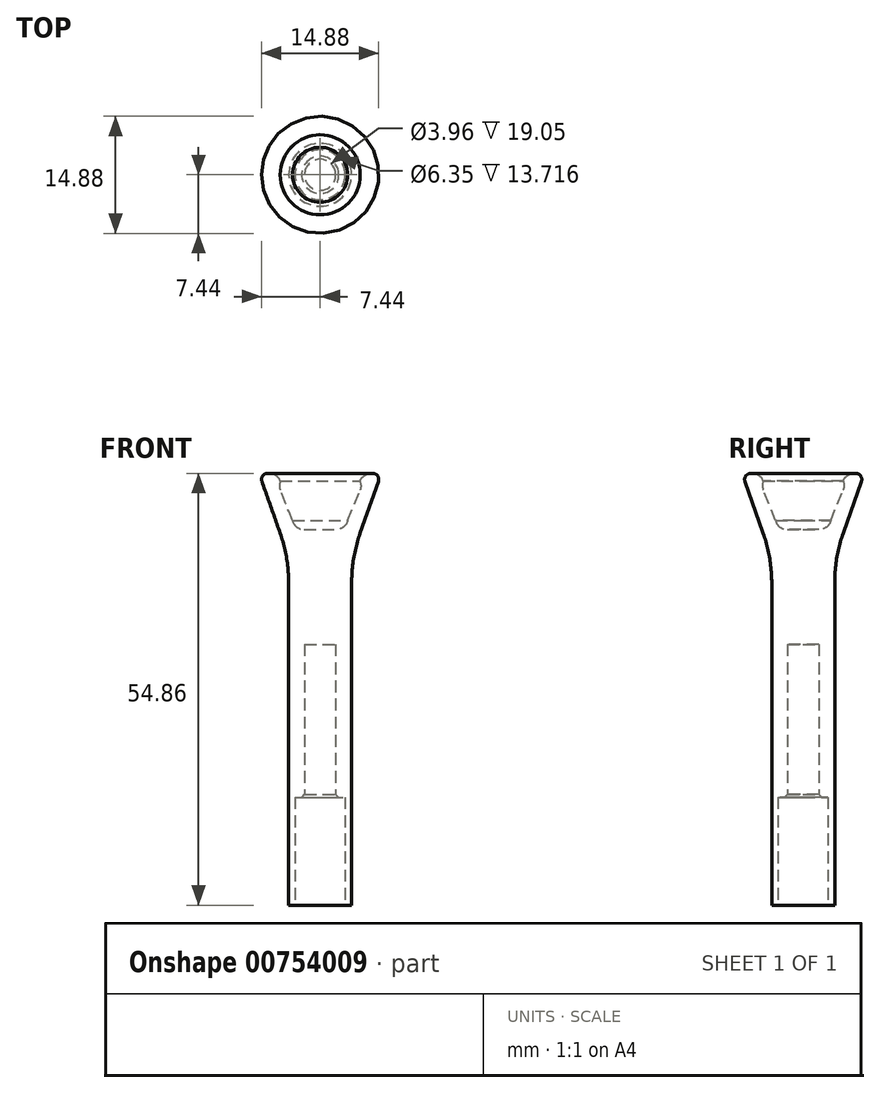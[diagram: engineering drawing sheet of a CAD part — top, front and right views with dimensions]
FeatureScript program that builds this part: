
annotation { "Feature Type Name" : "Feature", "Feature Type Description" : "" }
export const myFeature = defineFeature(function(context is Context, id is Id, definition is map)
    precondition{}
    {
        {
            var Q0;
            Q0=qCreatedBy(makeId("Front.planeOp"),FACE);
            var sketch = newSketch(context, id + "F0", { "sketchPlane" : qUnion([Q0])});
            skLineSegment(sketch, "E0", {"start": v(0, 0) * mm, "end": v(4, 0) * mm});
            skLineSegment(sketch, "E1", {"start": v(4, 0) * mm, "end": v(4, 40.94) * mm});
            skLineSegment(sketch, "E2", {"start": v(0.14, 46.68) * mm, "end": v(0, 46.68) * mm});
            skLineSegment(sketch, "E3", {"start": v(0, 46.68) * mm, "end": v(0, 60.15) * mm});
            skLineSegment(sketch, "E4", {"start": v(2.02, 47.72) * mm, "end": v(0, 47.72) * mm});
            skLineSegment(sketch, "E5", {"start": v(0, 47.72) * mm, "end": v(0, 0) * mm});
            skLineSegment(sketch, "E6", {"start": v(6.49, 54.86) * mm, "end": v(6.68, 54.86) * mm});
            skLineSegment(sketch, "E7", {"start": v(5.08, 47.27) * mm, "end": v(7.4, 53.85) * mm});
            skPoint(sketch, "E8.visualSharp", {"position": v(4, 44.2) * mm});
            skPoint(sketch, "E9.visualSharp", {"position": v(7.76, 54.86) * mm});
            skPoint(sketch, "E10.visualSharp", {"position": v(4.57, 54.86) * mm});
            skArc(sketch, "E10.filletArc", {"start": v(6.49, 54.86) * mm, "mid": v(5.64, 54.6) * mm, "end": v(5.08, 53.92) * mm});
            skPoint(sketch, "E11.visualSharp", {"position": v(3.2, 47.72) * mm});
            skArc(sketch, "E11.filletArc", {"start": v(2.02, 47.72) * mm, "mid": v(2.95, 48.04) * mm, "end": v(3.5, 48.86) * mm});
            skLineSegment(sketch, "E12", {"start": v(5.08, 53.92) * mm, "end": v(5.15, 53.43) * mm});
            skLineSegment(sketch, "E13", {"start": v(5.08, 52.76) * mm, "end": v(3.5, 48.86) * mm});
            skPoint(sketch, "E14.visualSharp", {"position": v(5.2, 53.09) * mm});
            skArc(sketch, "E14.filletArc", {"start": v(5.08, 52.76) * mm, "mid": v(5.16, 53.1) * mm, "end": v(5.15, 53.43) * mm});
            skLineSegment(sketch, "E15", {"start": v(0, 33.15) * mm, "end": v(1.98, 33.15) * mm});
            skLineSegment(sketch, "E16", {"start": v(1.98, 33.15) * mm, "end": v(1.98, 13.72) * mm});
            skLineSegment(sketch, "E17", {"start": v(1.98, 13.72) * mm, "end": v(3.18, 13.72) * mm});
            skLineSegment(sketch, "E18", {"start": v(3.18, 13.72) * mm, "end": v(3.18, 0) * mm});
            skArc(sketch, "E19.filletArc", {"start": v(5.08, 47.27) * mm, "mid": v(4.27, 44.15) * mm, "end": v(4, 40.94) * mm});
            skArc(sketch, "E20.filletArc", {"start": v(7.4, 53.85) * mm, "mid": v(7.3, 54.54) * mm, "end": v(6.68, 54.86) * mm});
            skSolve(sketch);
        }
        {
            var Q0;
            {var subQ3=sQuery(id+"F0.wireOp",EDGE,"E1");Q0=makeQuery(id+"F0.imprint","IMPRINT",FACE,{"disambiguationData":[TD([[makeQuery(id+"F0.imprint","IMPRINT",EDGE,{"derivedFrom":subQ3}),1.0]])]});}
            var Q1;
            Q1=sQuery(id+"F0.wireOp",EDGE,"E3");
            revolve(context, id + "F1", {"surfaceOperationType" : NewSurfaceOperationType.NEW, "entities" : qUnion([Q0]), "axis" : qUnion([Q1]), "revolveType" : RevolveType.FULL});
        }
        {
            var Q0;
            Q0=makeQuery(id+"F1.opRevolve","SWEPT_EDGE",EDGE,{"disambiguationData":[OSD([sQuery(id+"F0.wireOp",EDGE,"E16"),sQuery(id+"F0.wireOp",EDGE,"E17")])]});
            chamfer(context, id + "F2", {"entities" : qUnion([Q0]), "width" : 0.38 * mm, "tangentPropagation" : true});
        }
    });
